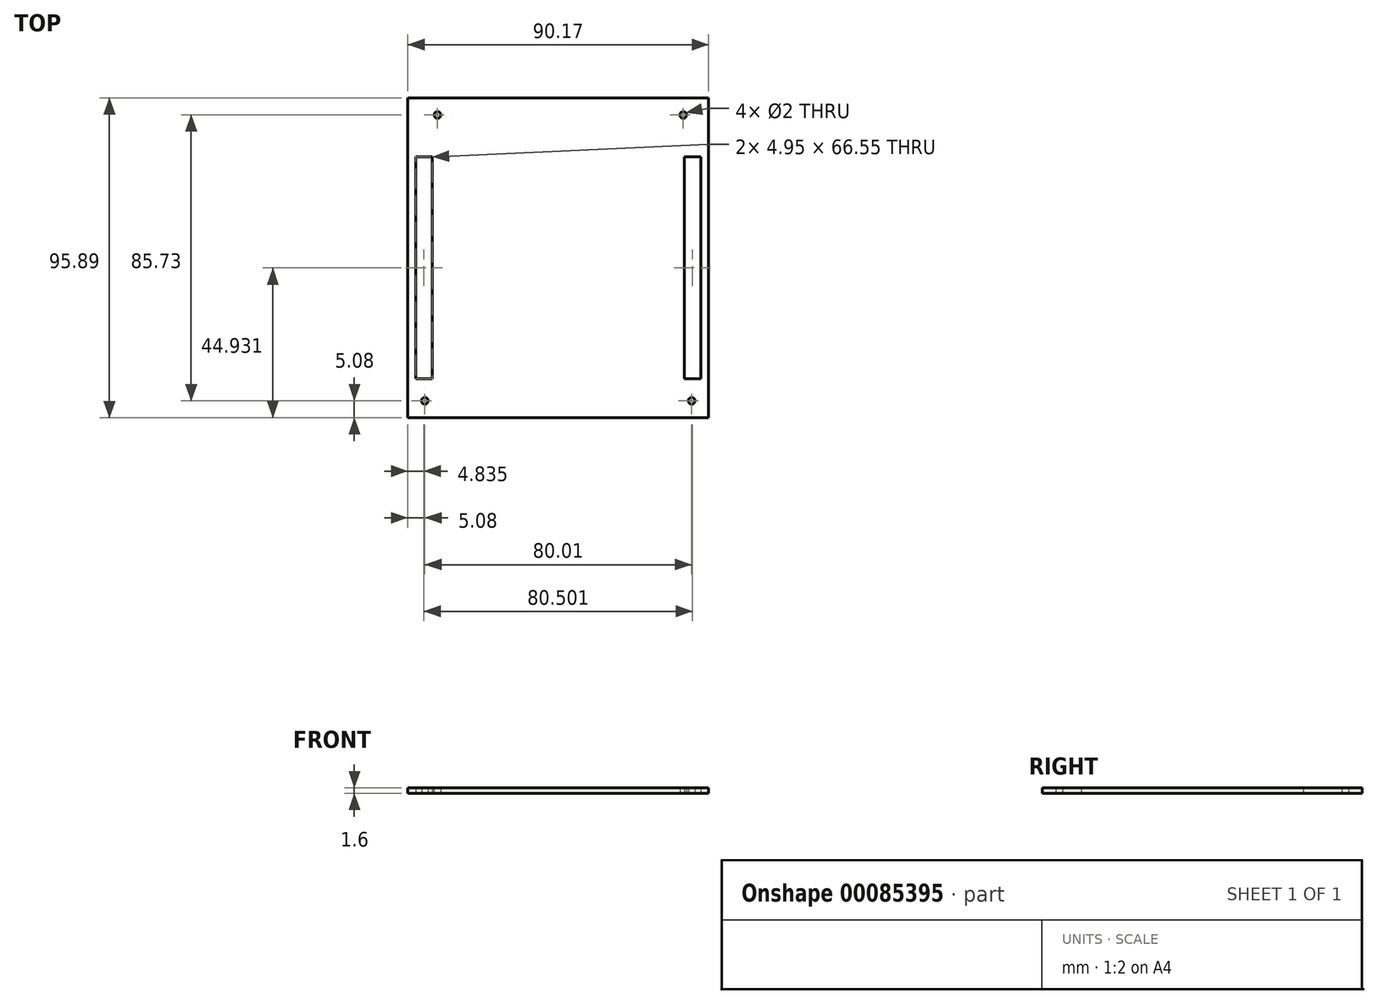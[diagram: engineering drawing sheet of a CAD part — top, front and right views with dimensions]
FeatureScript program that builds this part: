
annotation { "Feature Type Name" : "Feature", "Feature Type Description" : "" }
export const myFeature = defineFeature(function(context is Context, id is Id, definition is map)
    precondition{}
    {
        {
            var Q0;
            Q0=qCreatedBy(makeId("Top.planeOp"),FACE);
            var sketch = newSketch(context, id + "F0", { "sketchPlane" : qUnion([Q0])});
            skLineSegment(sketch, "E0.rect.bottom", {"start": v(-48.5, 47.4) * mm, "end": v(41.67, 47.4) * mm});
            skLineSegment(sketch, "E0.rect.top", {"start": v(-48.5, -48.5) * mm, "end": v(41.67, -48.5) * mm});
            skLineSegment(sketch, "E0.rect.left", {"start": v(-48.5, 47.4) * mm, "end": v(-48.5, -48.5) * mm});
            skLineSegment(sketch, "E0.rect.right", {"start": v(41.67, 47.4) * mm, "end": v(41.67, -48.5) * mm});
            skPoint(sketch, "E1", {"position": v(-43.42, -43.42) * mm});
            skPoint(sketch, "E2", {"position": v(36.59, -43.42) * mm});
            skPoint(sketch, "E3", {"position": v(34.05, 42.31) * mm});
            skPoint(sketch, "E4", {"position": v(-39.6, 42.31) * mm});
            skLineSegment(sketch, "E5.bottom", {"start": v(-41.19, -36.84) * mm, "end": v(-46.14, -36.84) * mm});
            skLineSegment(sketch, "E5.top", {"start": v(-41.19, 29.7) * mm, "end": v(-46.14, 29.7) * mm});
            skLineSegment(sketch, "E5.left", {"start": v(-41.19, -36.84) * mm, "end": v(-41.19, 29.7) * mm});
            skLineSegment(sketch, "E5.right", {"start": v(-46.14, -36.84) * mm, "end": v(-46.14, 29.7) * mm});
            skPoint(sketch, "E5.middle", {"position": v(-43.67, -3.57) * mm});
            skPoint(sketch, "E6", {"position": v(-3.41, 47.4) * mm});
            skPoint(sketch, "E7", {"position": v(-3.42, -48.5) * mm});
            skLineSegment(sketch, "E8", {"start": v(-3.41, 47.4) * mm, "end": v(-3.42, -48.5) * mm});
            skLineSegment(sketch, "E9.MirrorCS", {"start": v(34.36, 29.7) * mm, "end": v(39.31, 29.7) * mm});
            skLineSegment(sketch, "E10.MirrorCS", {"start": v(34.36, -36.84) * mm, "end": v(39.31, -36.84) * mm});
            skPoint(sketch, "E11.MirrorP", {"position": v(36.84, -3.57) * mm});
            skLineSegment(sketch, "E12.MirrorCS", {"start": v(34.36, -36.84) * mm, "end": v(34.36, 29.7) * mm});
            skLineSegment(sketch, "E13.MirrorCS", {"start": v(39.31, -36.84) * mm, "end": v(39.31, 29.7) * mm});
            skPoint(sketch, "E14", {"position": v(41.67, -0.55) * mm});
            skPoint(sketch, "E15", {"position": v(-48.5, -0.55) * mm});
            skLineSegment(sketch, "E16", {"start": v(-48.5, -0.55) * mm, "end": v(41.67, -0.55) * mm});
            skSolve(sketch);
        }
        {
            var Q0;
            Q0=makeQuery(id+"F0.imprint","IMPRINT",FACE,{"disambiguationData":[TD([[makeQuery(id+"F0.imprint","IMPRINT",EDGE,{"derivedFrom":sQuery(id+"F0.wireOp",EDGE,"E0.rect.bottom")}),-1.0]])]});
            var Q1;
            {var subQ1=sQuery(id+"F0.wireOp",EDGE,"E5.bottom");Q1=makeQuery(id+"F0.imprint","IMPRINT",FACE,{"disambiguationData":[TD([[makeQuery(id+"F0.imprint","IMPRINT",EDGE,{"derivedFrom":subQ1}),1.0]])]});}
            var Q2;
            {var subQ9=sQuery(id+"F0.wireOp",EDGE,"E10.MirrorCS");Q2=makeQuery(id+"F0.imprint","IMPRINT",FACE,{"disambiguationData":[TD([[makeQuery(id+"F0.imprint","IMPRINT",EDGE,{"derivedFrom":subQ9}),-1.0]])]});}
            extrude(context, id + "F1", {"entities" : qUnion([Q0, Q1, Q2]), "depth" : 1.6 * mm});
        }
        {
            var Q0;
            Q0=sQuery(id+"F0.wireOp",VERTEX,"E4");
            var Q1;
            Q1=sQuery(id+"F0.wireOp",VERTEX,"E1");
            var Q2;
            Q2=sQuery(id+"F0.wireOp",VERTEX,"E2");
            var Q3;
            Q3=sQuery(id+"F0.wireOp",VERTEX,"E3");
            var Q4;
            Q4=makeQuery(id+"F1.opExtrude","SWEPT_BODY",BODY,{"disambiguationData":[OSD([sQuery(id+"F0.wireOp",EDGE,"E0.rect.bottom"),sQuery(id+"F0.wireOp",EDGE,"E0.rect.top"),sQuery(id+"F0.wireOp",EDGE,"E0.rect.left"),sQuery(id+"F0.wireOp",EDGE,"E0.rect.right")])]});
            hole(context, id + "F2", {"style" : HoleStyle.SIMPLE, "endStyle" : HoleEndStyle.THROUGH, "oppositeDirection" : true, "holeDiameter" : 2 * mm, "locations" : qUnion([Q0, Q1, Q2, Q3]), "scope" : qUnion([Q4]), "isTappedThrough" : true});
        }
    });
